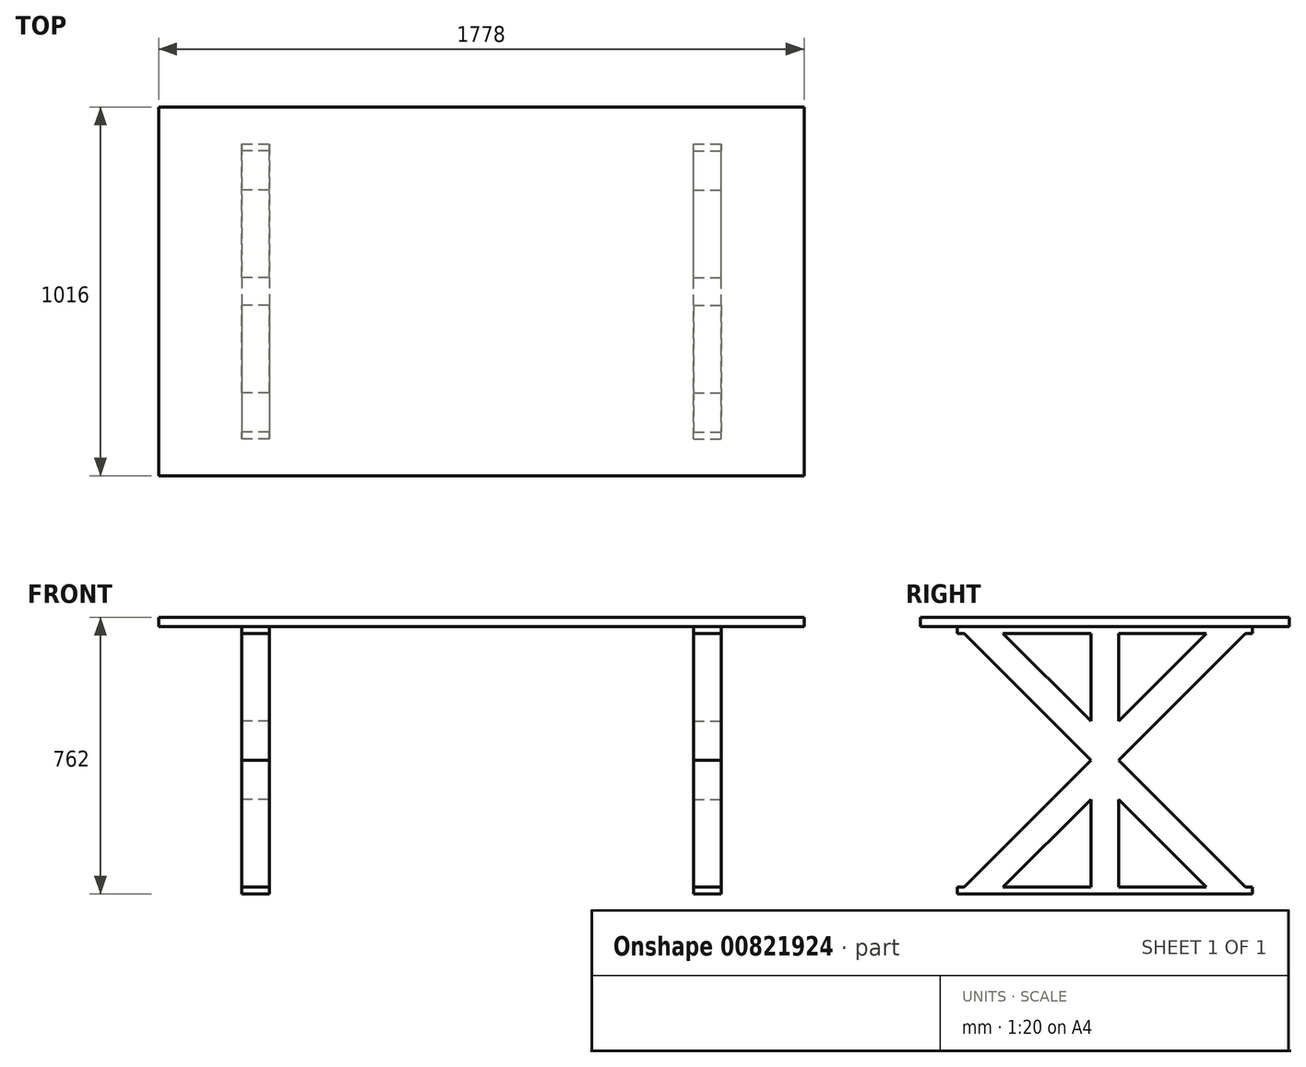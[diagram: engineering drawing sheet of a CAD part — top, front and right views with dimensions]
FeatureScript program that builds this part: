
annotation { "Feature Type Name" : "Feature", "Feature Type Description" : "" }
export const myFeature = defineFeature(function(context is Context, id is Id, definition is map)
    precondition{}
    {
        {
            var Q0;
            Q0=qCreatedBy(makeId("Top.planeOp"),FACE);
            var sketch = newSketch(context, id + "F0", { "sketchPlane" : qUnion([Q0])});
            skLineSegment(sketch, "E0.bottom", {"start": v(2.74, 0) * mm, "end": v(1780.74, 0) * mm});
            skLineSegment(sketch, "E0.top", {"start": v(2.74, 1016) * mm, "end": v(1780.74, 1016) * mm});
            skLineSegment(sketch, "E0.left", {"start": v(2.74, 0) * mm, "end": v(2.74, 1016) * mm});
            skLineSegment(sketch, "E0.right", {"start": v(1780.74, 0) * mm, "end": v(1780.74, 1016) * mm});
            skSolve(sketch);
        }
        {
            var Q0;
            Q0=makeQuery(id+"F0.imprint","IMPRINT",FACE,{"disambiguationData":[TD([[makeQuery(id+"F0.imprint","IMPRINT",EDGE,{"derivedFrom":sQuery(id+"F0.wireOp",EDGE,"E0.bottom")}),1.0]])]});
            extrude(context, id + "F1", {"entities" : qUnion([Q0]), "depth" : 25.4 * mm, "offsetDistance" : 25.4 * mm});
        }
        {
            var Q0;
            Q0=makeQuery(id+"F1.opExtrude","CAP_FACE",FACE,{"disambiguationData":[OSD([sQuery(id+"F0.wireOp",EDGE,"E0.bottom"),sQuery(id+"F0.wireOp",EDGE,"E0.top"),sQuery(id+"F0.wireOp",EDGE,"E0.left"),sQuery(id+"F0.wireOp",EDGE,"E0.right")])],"isStart":true});
            var sketch = newSketch(context, id + "F2", { "sketchPlane" : qUnion([Q0])});
            skLineSegment(sketch, "E1", {"start": v(2.74, -508) * mm, "end": v(1780.74, -508) * mm, "construction": true});
            skLineSegment(sketch, "E2.bottom", {"start": v(231.34, -546.1) * mm, "end": v(307.54, -546.1) * mm});
            skLineSegment(sketch, "E2.top", {"start": v(231.34, -469.9) * mm, "end": v(307.54, -469.9) * mm});
            skLineSegment(sketch, "E2.left", {"start": v(231.34, -546.1) * mm, "end": v(231.34, -469.9) * mm});
            skLineSegment(sketch, "E2.right", {"start": v(307.54, -546.1) * mm, "end": v(307.54, -469.9) * mm});
            skLineSegment(sketch, "E3.bottom", {"start": v(1475.94, -469.9) * mm, "end": v(1552.14, -469.9) * mm});
            skLineSegment(sketch, "E3.top", {"start": v(1475.94, -546.1) * mm, "end": v(1552.14, -546.1) * mm});
            skLineSegment(sketch, "E3.left", {"start": v(1475.94, -469.9) * mm, "end": v(1475.94, -546.1) * mm});
            skLineSegment(sketch, "E3.right", {"start": v(1552.14, -469.9) * mm, "end": v(1552.14, -546.1) * mm});
            skSolve(sketch);
        }
        {
            var Q0;
            Q0=makeQuery(id+"F2.imprint","IMPRINT",FACE,{"disambiguationData":[TD([[makeQuery(id+"F2.imprint","IMPRINT",EDGE,{"derivedFrom":sQuery(id+"F2.wireOp",EDGE,"E2.bottom")}),1.0]])]});
            var Q1;
            Q1=makeQuery(id+"F2.imprint","IMPRINT",FACE,{"disambiguationData":[TD([[makeQuery(id+"F2.imprint","IMPRINT",EDGE,{"derivedFrom":sQuery(id+"F2.wireOp",EDGE,"E3.bottom")}),-1.0]])]});
            extrude(context, id + "F3", {"entities" : qUnion([Q0, Q1]), "operationType" : NewBodyOperationType.ADD, "depth" : 717.55 * mm, "offsetDistance" : 25.4 * mm});
        }
        {
            var Q0;
            Q0=makeQuery(id+"F3.opExtrude","CAP_FACE",FACE,{"disambiguationData":[OSD([sQuery(id+"F2.wireOp",EDGE,"E2.bottom"),sQuery(id+"F2.wireOp",EDGE,"E2.top"),sQuery(id+"F2.wireOp",EDGE,"E2.left"),sQuery(id+"F2.wireOp",EDGE,"E2.right")])],"isStart":false});
            var sketch = newSketch(context, id + "F4", { "sketchPlane" : qUnion([Q0])});
            skLineSegment(sketch, "E4.bottom", {"start": v(231.34, -101.6) * mm, "end": v(307.54, -101.6) * mm});
            skLineSegment(sketch, "E4.top", {"start": v(231.34, -914.4) * mm, "end": v(307.54, -914.4) * mm});
            skLineSegment(sketch, "E4.left", {"start": v(231.34, -101.6) * mm, "end": v(231.34, -914.4) * mm});
            skLineSegment(sketch, "E4.right", {"start": v(307.54, -101.6) * mm, "end": v(307.54, -914.4) * mm});
            skPoint(sketch, "E5.0", {"position": v(1514.04, -546.1) * mm});
            skLineSegment(sketch, "E6.0.0", {"start": v(1475.94, -469.9) * mm, "end": v(1475.94, -546.1) * mm});
            skLineSegment(sketch, "E6.0.1", {"start": v(1475.94, -546.1) * mm, "end": v(1552.14, -546.1) * mm});
            skLineSegment(sketch, "E6.0.2", {"start": v(1552.14, -546.1) * mm, "end": v(1552.14, -469.9) * mm});
            skLineSegment(sketch, "E6.0.3", {"start": v(1552.14, -469.9) * mm, "end": v(1475.94, -469.9) * mm});
            skLineSegment(sketch, "E7.bottom", {"start": v(1475.94, -101.6) * mm, "end": v(1552.14, -101.6) * mm});
            skLineSegment(sketch, "E7.top", {"start": v(1475.94, -914.4) * mm, "end": v(1552.14, -914.4) * mm});
            skLineSegment(sketch, "E7.left", {"start": v(1475.94, -101.6) * mm, "end": v(1475.94, -914.4) * mm});
            skLineSegment(sketch, "E7.right", {"start": v(1552.14, -101.6) * mm, "end": v(1552.14, -914.4) * mm});
            skSolve(sketch);
        }
        {
            var Q0;
            {var subQ0=sQuery(id+"F4.wireOp",EDGE,"E4.bottom");Q0=makeQuery(id+"F4.imprint","IMPRINT",FACE,{"disambiguationData":[TD([[makeQuery(id+"F4.imprint","IMPRINT",EDGE,{"derivedFrom":subQ0}),-1.0]])]});}
            var Q1;
            {var subQ1=makeQuery(id+"F3.opExtrude","CAP_EDGE",EDGE,{"disambiguationData":[OSD([sQuery(id+"F2.wireOp",EDGE,"E2.bottom")])],"isStart":false});Q1=makeQuery(id+"F4.imprint","IMPRINT",FACE,{"disambiguationData":[TD([[makeQuery(id+"F4.imprint","IMPRINT",EDGE,{"derivedFrom":subQ1}),1.0]])]});}
            var Q2;
            {var subQ0=sQuery(id+"F4.wireOp",EDGE,"E4.top");Q2=makeQuery(id+"F4.imprint","IMPRINT",FACE,{"disambiguationData":[TD([[makeQuery(id+"F4.imprint","IMPRINT",EDGE,{"derivedFrom":subQ0}),1.0]])]});}
            var Q3;
            {var subQ0=sQuery(id+"F4.wireOp",EDGE,"E6.0.3");Q3=makeQuery(id+"F4.imprint","IMPRINT",FACE,{"disambiguationData":[TD([[makeQuery(id+"F4.imprint","IMPRINT",EDGE,{"derivedFrom":subQ0}),-1.0]])]});}
            var Q4;
            {var subQ0=sQuery(id+"F4.wireOp",EDGE,"E6.0.1");Q4=makeQuery(id+"F4.imprint","IMPRINT",FACE,{"disambiguationData":[TD([[makeQuery(id+"F4.imprint","IMPRINT",EDGE,{"derivedFrom":subQ0}),1.0]])]});}
            var Q5;
            {var subQ0=sQuery(id+"F4.wireOp",EDGE,"E6.0.1");Q5=makeQuery(id+"F4.imprint","IMPRINT",FACE,{"disambiguationData":[TD([[makeQuery(id+"F4.imprint","IMPRINT",EDGE,{"derivedFrom":subQ0}),-1.0]])]});}
            extrude(context, id + "F5", {"entities" : qUnion([Q0, Q1, Q2, Q3, Q4, Q5]), "operationType" : NewBodyOperationType.ADD, "depth" : 19.05 * mm, "offsetDistance" : 25.4 * mm});
        }
        {
            var Q0;
            Q0=makeQuery(id+"F1.opExtrude","CAP_FACE",FACE,{"disambiguationData":[OSD([sQuery(id+"F0.wireOp",EDGE,"E0.bottom"),sQuery(id+"F0.wireOp",EDGE,"E0.top"),sQuery(id+"F0.wireOp",EDGE,"E0.left"),sQuery(id+"F0.wireOp",EDGE,"E0.right")])],"isStart":true});
            var sketch = newSketch(context, id + "F6", { "sketchPlane" : qUnion([Q0])});
            skLineSegment(sketch, "E8.0.0", {"start": v(307.54, -914.4) * mm, "end": v(307.54, -101.6) * mm});
            skLineSegment(sketch, "E8.0.1", {"start": v(307.54, -101.6) * mm, "end": v(231.34, -101.6) * mm});
            skLineSegment(sketch, "E8.0.2", {"start": v(231.34, -101.6) * mm, "end": v(231.34, -914.4) * mm});
            skLineSegment(sketch, "E8.0.3", {"start": v(231.34, -914.4) * mm, "end": v(307.54, -914.4) * mm});
            skLineSegment(sketch, "E9.0.0", {"start": v(1552.14, -914.4) * mm, "end": v(1552.14, -101.6) * mm});
            skLineSegment(sketch, "E9.0.1", {"start": v(1552.14, -101.6) * mm, "end": v(1475.94, -101.6) * mm});
            skLineSegment(sketch, "E9.0.2", {"start": v(1475.94, -101.6) * mm, "end": v(1475.94, -914.4) * mm});
            skLineSegment(sketch, "E9.0.3", {"start": v(1475.94, -914.4) * mm, "end": v(1552.14, -914.4) * mm});
            skSolve(sketch);
        }
        {
            var Q0;
            {var subQ2=sQuery(id+"F6.wireOp",EDGE,"E9.0.3");Q0=makeQuery(id+"F6.imprint","IMPRINT",FACE,{"disambiguationData":[TD([[makeQuery(id+"F6.imprint","IMPRINT",EDGE,{"derivedFrom":subQ2}),1.0]])]});}
            var Q1;
            {var subQ2=sQuery(id+"F6.wireOp",EDGE,"E9.0.1");Q1=makeQuery(id+"F6.imprint","IMPRINT",FACE,{"disambiguationData":[TD([[makeQuery(id+"F6.imprint","IMPRINT",EDGE,{"derivedFrom":subQ2}),1.0]])]});}
            var Q2;
            {var subQ2=sQuery(id+"F6.wireOp",EDGE,"E8.0.3");Q2=makeQuery(id+"F6.imprint","IMPRINT",FACE,{"disambiguationData":[TD([[makeQuery(id+"F6.imprint","IMPRINT",EDGE,{"derivedFrom":subQ2}),1.0]])]});}
            var Q3;
            {var subQ2=sQuery(id+"F6.wireOp",EDGE,"E8.0.1");Q3=makeQuery(id+"F6.imprint","IMPRINT",FACE,{"disambiguationData":[TD([[makeQuery(id+"F6.imprint","IMPRINT",EDGE,{"derivedFrom":subQ2}),1.0]])]});}
            extrude(context, id + "F7", {"entities" : qUnion([Q0, Q1, Q2, Q3]), "operationType" : NewBodyOperationType.ADD, "depth" : 19.05 * mm, "offsetDistance" : 25.4 * mm});
        }
        {
            var Q0;
            {var subQ0=sQuery(id+"F6.wireOp",EDGE,"E8.0.2");Q0=makeQuery(id+"F7.boolean.opBoolean","MERGE",FACE,{"derivedFrom":[makeQuery(id+"F5.boolean.opBoolean","MERGE",FACE,{"derivedFrom":[makeQuery(id+"F3.opExtrude","SWEPT_FACE",FACE,{"disambiguationData":[OSD([sQuery(id+"F2.wireOp",EDGE,"E2.left")])]}),makeQuery(id+"F5.opExtrude","SWEPT_FACE",FACE,{"disambiguationData":[OSD([sQuery(id+"F4.wireOp",EDGE,"E4.left")])]})]}),makeQuery(id+"F7.opExtrude","SWEPT_FACE",FACE,{"disambiguationData":[OSD([subQ0]),TDD([makeQuery(id+"F6.imprint","IMPRINT",EDGE,{"disambiguationData":[TD([[makeQuery(id+"F6.imprint","INTERSECT",VERTEX,{"derivedFrom":[makeQuery(id+"F3.opExtrude","CAP_EDGE",EDGE,{"disambiguationData":[OSD([sQuery(id+"F2.wireOp",EDGE,"E2.top")])],"isStart":true}),subQ0]}),1.0],[makeQuery(id+"F6.imprint","INTERSECT",VERTEX,{"derivedFrom":[sQuery(id+"F6.wireOp",EDGE,"E8.0.1"),subQ0]}),-1.0]])],"derivedFrom":subQ0})])]}),makeQuery(id+"F7.opExtrude","SWEPT_FACE",FACE,{"disambiguationData":[OSD([subQ0]),TDD([makeQuery(id+"F6.imprint","IMPRINT",EDGE,{"disambiguationData":[TD([[makeQuery(id+"F6.imprint","INTERSECT",VERTEX,{"derivedFrom":[makeQuery(id+"F3.opExtrude","CAP_EDGE",EDGE,{"disambiguationData":[OSD([sQuery(id+"F2.wireOp",EDGE,"E2.bottom")])],"isStart":true}),subQ0]}),-1.0],[makeQuery(id+"F6.imprint","INTERSECT",VERTEX,{"derivedFrom":[subQ0,sQuery(id+"F6.wireOp",EDGE,"E8.0.3")]}),1.0]])],"derivedFrom":subQ0})])]})]});}
            var sketch = newSketch(context, id + "F8", { "sketchPlane" : qUnion([Q0])});
            skLineSegment(sketch, "E10", {"start": v(-546.1, -368.3) * mm, "end": v(-469.9, -368.3) * mm, "construction": true});
            skLineSegment(sketch, "E11", {"start": v(-546.1, -368.3) * mm, "end": v(-895.35, -19.05) * mm});
            skLineSegment(sketch, "E12", {"start": v(-546.1, -260.54) * mm, "end": v(-787.59, -19.05) * mm});
            skLineSegment(sketch, "E13", {"start": v(-508, -736.6) * mm, "end": v(-508, 0) * mm, "construction": true});
            skLineSegment(sketch, "E14.MirrorCS", {"start": v(-546.1, -368.3) * mm, "end": v(-895.35, -717.55) * mm});
            skLineSegment(sketch, "E15.MirrorCS", {"start": v(-546.1, -476.06) * mm, "end": v(-787.59, -717.55) * mm});
            skLineSegment(sketch, "E16.MirrorCS", {"start": v(-469.9, -260.54) * mm, "end": v(-228.41, -19.05) * mm});
            skLineSegment(sketch, "E17.MirrorCS", {"start": v(-469.9, -368.3) * mm, "end": v(-120.65, -19.05) * mm});
            skLineSegment(sketch, "E18.MirrorCS", {"start": v(-469.9, -368.3) * mm, "end": v(-120.65, -717.55) * mm});
            skLineSegment(sketch, "E19.MirrorCS", {"start": v(-469.9, -476.06) * mm, "end": v(-228.41, -717.55) * mm});
            skLineSegment(sketch, "E20", {"start": v(-895.35, -19.05) * mm, "end": v(-787.59, -19.05) * mm});
            skLineSegment(sketch, "E21", {"start": v(-228.41, -19.05) * mm, "end": v(-120.65, -19.05) * mm});
            skLineSegment(sketch, "E22", {"start": v(-895.35, -717.55) * mm, "end": v(-787.59, -717.55) * mm});
            skLineSegment(sketch, "E23", {"start": v(-228.41, -717.55) * mm, "end": v(-120.65, -717.55) * mm});
            skSolve(sketch);
        }
        {
            var Q0;
            {var subQ0=sQuery(id+"F8.wireOp",EDGE,"E11");Q0=makeQuery(id+"F8.imprint","IMPRINT",FACE,{"disambiguationData":[TD([[makeQuery(id+"F8.imprint","IMPRINT",EDGE,{"derivedFrom":subQ0}),-1.0]])]});}
            var Q1;
            {var subQ0=sQuery(id+"F8.wireOp",EDGE,"E16.MirrorCS");Q1=makeQuery(id+"F8.imprint","IMPRINT",FACE,{"disambiguationData":[TD([[makeQuery(id+"F8.imprint","IMPRINT",EDGE,{"derivedFrom":subQ0}),-1.0]])]});}
            var Q2;
            {var subQ0=sQuery(id+"F8.wireOp",EDGE,"E18.MirrorCS");Q2=makeQuery(id+"F8.imprint","IMPRINT",FACE,{"disambiguationData":[TD([[makeQuery(id+"F8.imprint","IMPRINT",EDGE,{"derivedFrom":subQ0}),-1.0]])]});}
            var Q3;
            {var subQ0=sQuery(id+"F8.wireOp",EDGE,"E14.MirrorCS");Q3=makeQuery(id+"F8.imprint","IMPRINT",FACE,{"disambiguationData":[TD([[makeQuery(id+"F8.imprint","IMPRINT",EDGE,{"derivedFrom":subQ0}),1.0]])]});}
            extrude(context, id + "F9", {"entities" : qUnion([Q0, Q1, Q2, Q3]), "operationType" : NewBodyOperationType.ADD, "oppositeDirection" : true, "depth" : 76.2 * mm, "offsetDistance" : 25.4 * mm});
        }
        {
            var Q0;
            {var subQ0=sQuery(id+"F6.wireOp",EDGE,"E9.0.0");Q0=makeQuery(id+"F7.boolean.opBoolean","MERGE",FACE,{"derivedFrom":[makeQuery(id+"F5.boolean.opBoolean","MERGE",FACE,{"derivedFrom":[makeQuery(id+"F3.opExtrude","SWEPT_FACE",FACE,{"disambiguationData":[OSD([sQuery(id+"F2.wireOp",EDGE,"E3.right")])]}),makeQuery(id+"F5.opExtrude","SWEPT_FACE",FACE,{"disambiguationData":[OSD([sQuery(id+"F4.wireOp",EDGE,"E7.right")])]})]}),makeQuery(id+"F7.opExtrude","SWEPT_FACE",FACE,{"disambiguationData":[OSD([subQ0]),TDD([makeQuery(id+"F6.imprint","IMPRINT",EDGE,{"disambiguationData":[TD([[makeQuery(id+"F6.imprint","INTERSECT",VERTEX,{"derivedFrom":[makeQuery(id+"F3.opExtrude","CAP_EDGE",EDGE,{"disambiguationData":[OSD([sQuery(id+"F2.wireOp",EDGE,"E3.top")])],"isStart":true}),subQ0]}),1.0],[makeQuery(id+"F6.imprint","INTERSECT",VERTEX,{"derivedFrom":[subQ0,sQuery(id+"F6.wireOp",EDGE,"E9.0.3")]}),-1.0]])],"derivedFrom":subQ0})])]}),makeQuery(id+"F7.opExtrude","SWEPT_FACE",FACE,{"disambiguationData":[OSD([subQ0]),TDD([makeQuery(id+"F6.imprint","IMPRINT",EDGE,{"disambiguationData":[TD([[makeQuery(id+"F6.imprint","INTERSECT",VERTEX,{"derivedFrom":[makeQuery(id+"F3.opExtrude","CAP_EDGE",EDGE,{"disambiguationData":[OSD([sQuery(id+"F2.wireOp",EDGE,"E3.bottom")])],"isStart":true}),subQ0]}),-1.0],[makeQuery(id+"F6.imprint","INTERSECT",VERTEX,{"derivedFrom":[subQ0,sQuery(id+"F6.wireOp",EDGE,"E9.0.1")]}),1.0]])],"derivedFrom":subQ0})])]})]});}
            var sketch = newSketch(context, id + "F10", { "sketchPlane" : qUnion([Q0])});
            skLineSegment(sketch, "E24.0", {"start": v(469.9, -368.3) * mm, "end": v(120.65, -19.05) * mm});
            skLineSegment(sketch, "E25.0", {"start": v(469.9, -260.54) * mm, "end": v(228.41, -19.05) * mm});
            skLineSegment(sketch, "E26.0", {"start": v(546.1, -260.54) * mm, "end": v(787.59, -19.05) * mm});
            skLineSegment(sketch, "E27.0", {"start": v(546.1, -368.3) * mm, "end": v(895.35, -19.05) * mm});
            skLineSegment(sketch, "E28.0", {"start": v(469.9, -368.3) * mm, "end": v(120.65, -717.55) * mm});
            skLineSegment(sketch, "E29.0", {"start": v(469.9, -476.06) * mm, "end": v(228.41, -717.55) * mm});
            skLineSegment(sketch, "E30.0", {"start": v(546.1, -476.06) * mm, "end": v(787.59, -717.55) * mm});
            skLineSegment(sketch, "E31.0", {"start": v(546.1, -368.3) * mm, "end": v(895.35, -717.55) * mm});
            skSolve(sketch);
        }
        {
            var Q0;
            {var subQ0=sQuery(id+"F10.wireOp",EDGE,"E24.0");Q0=makeQuery(id+"F10.imprint","IMPRINT",FACE,{"disambiguationData":[TD([[makeQuery(id+"F10.imprint","IMPRINT",EDGE,{"derivedFrom":subQ0}),-1.0]])]});}
            var Q1;
            {var subQ0=sQuery(id+"F10.wireOp",EDGE,"E26.0");Q1=makeQuery(id+"F10.imprint","IMPRINT",FACE,{"disambiguationData":[TD([[makeQuery(id+"F10.imprint","IMPRINT",EDGE,{"derivedFrom":subQ0}),-1.0]])]});}
            var Q2;
            {var subQ0=sQuery(id+"F10.wireOp",EDGE,"E30.0");Q2=makeQuery(id+"F10.imprint","IMPRINT",FACE,{"disambiguationData":[TD([[makeQuery(id+"F10.imprint","IMPRINT",EDGE,{"derivedFrom":subQ0}),1.0]])]});}
            var Q3;
            {var subQ0=sQuery(id+"F10.wireOp",EDGE,"E28.0");Q3=makeQuery(id+"F10.imprint","IMPRINT",FACE,{"disambiguationData":[TD([[makeQuery(id+"F10.imprint","IMPRINT",EDGE,{"derivedFrom":subQ0}),1.0]])]});}
            extrude(context, id + "F11", {"entities" : qUnion([Q0, Q1, Q2, Q3]), "operationType" : NewBodyOperationType.ADD, "oppositeDirection" : true, "depth" : 76.2 * mm, "offsetDistance" : 25.4 * mm});
        }
    });
